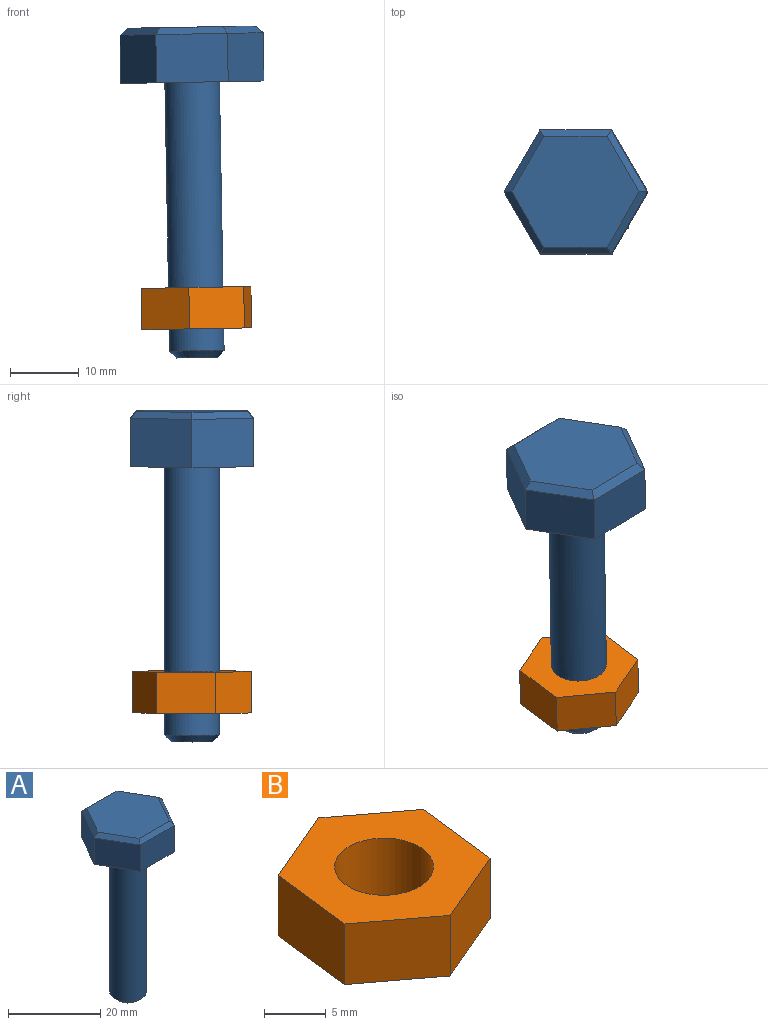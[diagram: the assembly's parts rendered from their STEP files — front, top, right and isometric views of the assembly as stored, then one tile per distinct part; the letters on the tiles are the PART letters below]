
ASSEMBLY  parts=2 mates=1
PART A: 17 faces, bbox 20.8x18x48 mm
  f0: plane 9x7mm, normal (0.87,0.5,0), area 72.7mm2, adj f1,f5,f6,f12
  f1: plane 10.39x7mm, normal (0,1,0), area 72.7mm2, adj f0,f2,f6,f10
  f2: plane 9x7mm, normal (-0.87,0.5,0), area 72.7mm2, adj f1,f3,f6,f11
  f3: plane 9x7mm, normal (-0.87,-0.5,0), area 72.7mm2, adj f2,f4,f6,f13
  f4: plane 10.39x7mm, normal (0,-1,0), area 72.7mm2, adj f3,f5,f6,f15
  f5: plane 9x7mm, normal (0.87,-0.5,0), area 72.7mm2, adj f0,f4,f6,f14
  f6: plane 20.78x18mm, normal (0,0,-1), area 230.3mm2, adj f0,f1,f2,f3,f4,f5,f8
  f7: plane 18.48x16mm, normal (0,0,1), area 221.7mm2, adj f10,f11,f12,f13,f14,f15
  f8: cylinder r=4mm len=39mm, axis (0,0,1), area 980.2mm2, adj f6,f16
  f9: plane 6x6mm, normal (0,0,-1), area 28.3mm2, adj f16
  f10: plane 10.39x1mm, normal (0,0.71,0.71), area 13.9mm2, adj f1,f7,f11,f12
  f11: plane 9x5.77mm, normal (-0.61,0.35,0.71), area 13.9mm2, adj f2,f7,f10,f13
  f12: plane 9x5.77mm, normal (0.61,0.35,0.71), area 13.9mm2, adj f0,f7,f10,f14
  f13: plane 9x5.77mm, normal (-0.61,-0.35,0.71), area 13.9mm2, adj f3,f7,f11,f15
  f14: plane 9x5.77mm, normal (0.61,-0.35,0.71), area 13.9mm2, adj f5,f7,f12,f15
  f15: plane 10.39x1mm, normal (0,-0.71,0.71), area 13.9mm2, adj f4,f7,f13,f14
  f16: cone r=3mm half-angle=45deg, axis (0,0,1), area 31.1mm2, adj f8,f9
PART B: 9 faces, bbox 15.9x17.2x6 mm
  f0: plane 7.97x6mm, normal (-0.39,0.92,0), area 52mm2, adj f1,f5,f6,f7
  f1: plane 6.93x6mm, normal (0.6,0.8,0), area 52mm2, adj f0,f2,f6,f7
  f2: plane 8.6x6mm, normal (0.99,-0.12,0), area 52mm2, adj f1,f3,f6,f7
  f3: plane 7.97x6mm, normal (0.39,-0.92,0), area 52mm2, adj f2,f4,f6,f7
  f4: plane 6.93x6mm, normal (-0.6,-0.8,0), area 52mm2, adj f3,f5,f6,f7
  f5: plane 8.6x6mm, normal (-0.99,0.12,0), area 52mm2, adj f0,f4,f6,f7
  f6: plane 17.2x15.93mm, normal (0,0,-1), area 144.6mm2, adj f0,f1,f2,f3,f4,f5,f8
  f7: plane 17.2x15.93mm, normal (0,0,1), area 144.6mm2, adj f0,f1,f2,f3,f4,f5,f8
  f8: cylinder r=4mm len=8mm, axis (0,0,-1), area 150.8mm2, adj f6,f7
PLACE A rot(axis=(0,-1,0),1deg) t=(-24.27,-24.34,21.81)mm
PLACE B rot(axis=(0,-1,0),1deg) t=(-24.88,-24.34,57)mm
MATE cylindrical B.f8 <-> A.f8  axis (0.02,0,-1) through (-23.5,-24.34,-21.99)mm
